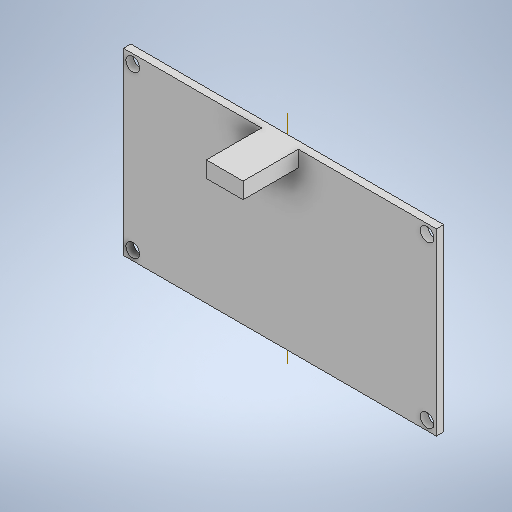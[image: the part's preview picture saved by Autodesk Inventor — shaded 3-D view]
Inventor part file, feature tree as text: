
AUTODESK INVENTOR PART (.ipt)
format: ipt  version: 2025 (Build 290162000, 162)  size: 250,368 bytes
history: native  units: in
note: dims shown in document units (in); Inventor stores cm internally (conversion verified against a paired STEP export)
features: extrude x3, sketch x3, other x1
ambient origin geometry x8: Origin, YZ Plane, XZ Plane, XY Plane, X Axis, Y Axis, Z Axis, Center Point
bodies: Body1 (feature_tree)
feature tree (7):
  other  "솔리드1"
  extrude  "돌출1"  Depth=2.6772in
  extrude  "돌출2"  Depth=1.5354in
  extrude  "돌출3"  Depth=0.063in TaperAngle=0.0deg
  sketch  "스케치1"
  sketch  "스케치3"
  sketch  "스케치4"
